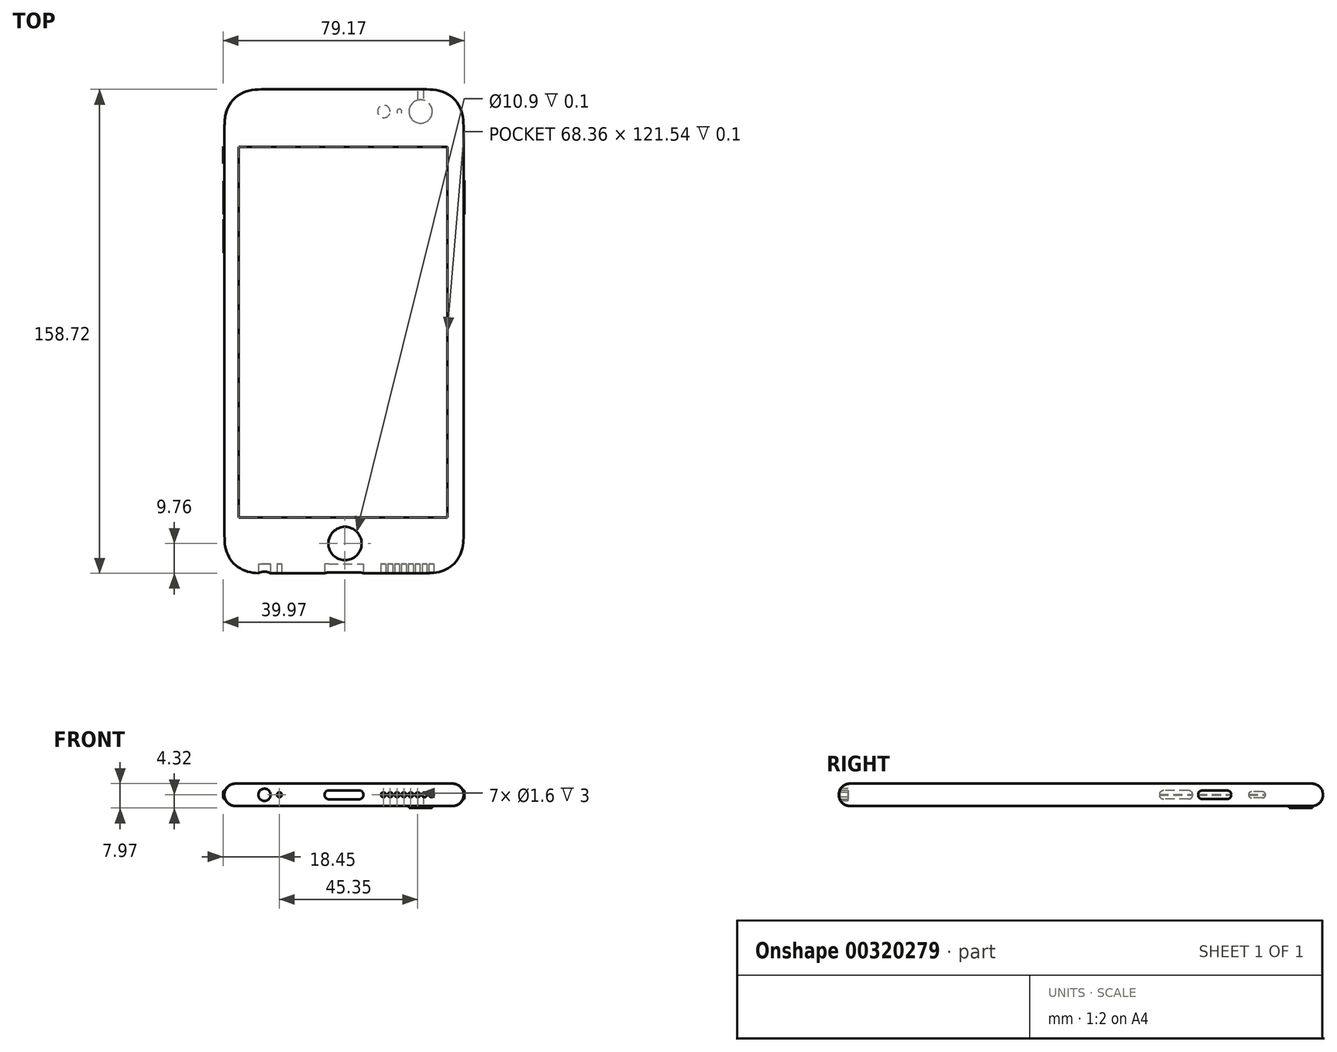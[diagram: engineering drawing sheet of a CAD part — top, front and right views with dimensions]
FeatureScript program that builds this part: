
annotation { "Feature Type Name" : "Feature", "Feature Type Description" : "" }
export const myFeature = defineFeature(function(context is Context, id is Id, definition is map)
    precondition{}
    {
        {
            var Q0;
            Q0=qCreatedBy(makeId("Top.planeOp"),FACE);
            var sketch = newSketch(context, id + "F0", { "sketchPlane" : qUnion([Q0])});
            skLineSegment(sketch, "E0.rect.bottom", {"start": v(25.09, -79.36) * mm, "end": v(-25.09, -79.36) * mm});
            skLineSegment(sketch, "E0.rect.top", {"start": v(25.09, 79.36) * mm, "end": v(-25.09, 79.36) * mm});
            skLineSegment(sketch, "E0.rect.left", {"start": v(39.22, -65.23) * mm, "end": v(39.22, 65.23) * mm});
            skLineSegment(sketch, "E0.rect.right", {"start": v(-39.22, -65.23) * mm, "end": v(-39.22, 65.23) * mm});
            skPoint(sketch, "E0.rect.middle", {"position": v(0, 0) * mm});
            skCircle(sketch, "E1", {"center": v(25.12, 72.09) * mm, "radius": 3.83 * mm});
            skCircle(sketch, "E2", {"center": v(18.16, 72.09) * mm, "radius": 0.8 * mm});
            skCircle(sketch, "E3", {"center": v(13.06, 72.09) * mm, "radius": 2.06 * mm});
            skLineSegment(sketch, "E4", {"start": v(-39.22, 72.1) * mm, "end": v(39.22, 72.1) * mm, "construction": true});
            skPoint(sketch, "E5.visualSharp", {"position": v(-39.22, 79.36) * mm});
            skFitSpline(sketch, "E6", {"points": [v(-25.09, 79.36) * mm, v(-29.02, 79.25) * mm, v(-32.83, 78.38) * mm, v(-36.09, 76.23) * mm, v(-38.24, 72.97) * mm, v(-39.1, 69.16) * mm, v(-39.22, 65.23) * mm], "startDerivative": vector(-8.98, 0) * mm, "endDerivative": vector(0, -8.98) * mm});
            skLineSegment(sketch, "E7", {"start": v(-25.09, 79.36) * mm, "end": v(-39.22, 79.36) * mm, "construction": true});
            skLineSegment(sketch, "E8", {"start": v(-39.22, 79.36) * mm, "end": v(-39.22, 65.23) * mm, "construction": true});
            skLineSegment(sketch, "E9", {"start": v(0, 79.36) * mm, "end": v(0, -79.36) * mm, "construction": true});
            skLineSegment(sketch, "E10", {"start": v(-39.22, 0) * mm, "end": v(39.22, 0) * mm, "construction": true});
            skFitSpline(sketch, "E11.MirrorCS", {"points": [v(25.09, 79.36) * mm, v(29.02, 79.25) * mm, v(32.83, 78.38) * mm, v(36.09, 76.23) * mm, v(38.24, 72.97) * mm, v(39.1, 69.16) * mm, v(39.22, 65.23) * mm], "startDerivative": vector(8.98, 0) * mm, "endDerivative": vector(0, -8.98) * mm});
            skFitSpline(sketch, "E12.MirrorCS", {"points": [v(-25.09, -79.36) * mm, v(-29.02, -79.25) * mm, v(-32.83, -78.38) * mm, v(-36.09, -76.23) * mm, v(-38.24, -72.97) * mm, v(-39.1, -69.16) * mm, v(-39.22, -65.23) * mm], "startDerivative": vector(-8.98, 0) * mm, "endDerivative": vector(0, 8.98) * mm});
            skFitSpline(sketch, "E13.MirrorCS", {"points": [v(25.09, -79.36) * mm, v(29.02, -79.25) * mm, v(32.83, -78.38) * mm, v(36.09, -76.23) * mm, v(38.24, -72.97) * mm, v(39.1, -69.16) * mm, v(39.22, -65.23) * mm], "startDerivative": vector(8.98, 0) * mm, "endDerivative": vector(0, 8.98) * mm});
            skCircle(sketch, "E14", {"center": v(0, 37.36) * mm, "radius": 11 * mm, "construction": true});
            skSolve(sketch);
        }
        {
            var Q0;
            Q0=makeQuery(id+"F0.imprint","IMPRINT",FACE,{"disambiguationData":[TD([[makeQuery(id+"F0.imprint","IMPRINT",EDGE,{"derivedFrom":sQuery(id+"F0.wireOp",EDGE,"E0.rect.bottom")}),-1.0]])]});
            var Q1;
            Q1=makeQuery(id+"F0.imprint","IMPRINT",FACE,{"disambiguationData":[TD([[makeQuery(id+"F0.imprint","IMPRINT",EDGE,{"derivedFrom":sQuery(id+"F0.wireOp",EDGE,"E1")}),1.0]])]});
            var Q2;
            Q2=makeQuery(id+"F0.imprint","IMPRINT",FACE,{"disambiguationData":[TD([[makeQuery(id+"F0.imprint","IMPRINT",EDGE,{"derivedFrom":sQuery(id+"F0.wireOp",EDGE,"E2")}),1.0]])]});
            var Q3;
            Q3=makeQuery(id+"F0.imprint","IMPRINT",FACE,{"disambiguationData":[TD([[makeQuery(id+"F0.imprint","IMPRINT",EDGE,{"derivedFrom":sQuery(id+"F0.wireOp",EDGE,"E3")}),1.0]])]});
            extrude(context, id + "F1", {"entities" : qUnion([Q0, Q1, Q2, Q3]), "depth" : 7.3 * mm});
        }
        {
            var Q0;
            Q0=makeQuery(id+"F0.imprint","IMPRINT",FACE,{"disambiguationData":[TD([[makeQuery(id+"F0.imprint","IMPRINT",EDGE,{"derivedFrom":sQuery(id+"F0.wireOp",EDGE,"E1")}),1.0]])]});
            extrude(context, id + "F2", {"entities" : qUnion([Q0]), "operationType" : NewBodyOperationType.ADD, "oppositeDirection" : true, "depth" : 0.67 * mm});
        }
        {
            var Q0;
            Q0=makeQuery(id+"F0.imprint","IMPRINT",FACE,{"disambiguationData":[TD([[makeQuery(id+"F0.imprint","IMPRINT",EDGE,{"derivedFrom":sQuery(id+"F0.wireOp",EDGE,"E3")}),1.0]])]});
            var Q1;
            Q1=makeQuery(id+"F0.imprint","IMPRINT",FACE,{"disambiguationData":[TD([[makeQuery(id+"F0.imprint","IMPRINT",EDGE,{"derivedFrom":sQuery(id+"F0.wireOp",EDGE,"E2")}),1.0]])]});
            extrude(context, id + "F3", {"entities" : qUnion([Q0, Q1]), "operationType" : NewBodyOperationType.REMOVE, "depth" : 0.1 * mm});
        }
        {
            var Q0;
            Q0=makeQuery(id+"F1.opExtrude","CAP_FACE",FACE,{"disambiguationData":[OSD([sQuery(id+"F0.wireOp",EDGE,"E0.rect.bottom"),sQuery(id+"F0.wireOp",EDGE,"E0.rect.top"),sQuery(id+"F0.wireOp",EDGE,"E0.rect.left"),sQuery(id+"F0.wireOp",EDGE,"E0.rect.right"),sQuery(id+"F0.wireOp",EDGE,"d7852d5b-fe0f-4a90-bdf2-04cff158e1f8.filletArc"),sQuery(id+"F0.wireOp",EDGE,"E5.filletArc"),sQuery(id+"F0.wireOp",EDGE,"7c06d2e9-cdf6-4879-9dee-aab3bc7c6033.filletArc"),sQuery(id+"F0.wireOp",EDGE,"93b3bdb9-dbb8-49f8-8f1e-002f612095da.filletArc")])],"isStart":false});
            var sketch = newSketch(context, id + "F4", { "sketchPlane" : qUnion([Q0])});
            skCircle(sketch, "E15", {"center": v(0.32, -69.6) * mm, "radius": 5.45 * mm});
            skLineSegment(sketch, "E16.bottom", {"start": v(-34.51, 60.44) * mm, "end": v(33.85, 60.44) * mm});
            skLineSegment(sketch, "E16.top", {"start": v(-34.5, -61.1) * mm, "end": v(33.85, -61.1) * mm});
            skLineSegment(sketch, "E16.left", {"start": v(-34.51, 60.44) * mm, "end": v(-34.5, -61.1) * mm});
            skLineSegment(sketch, "E16.right", {"start": v(33.85, 60.44) * mm, "end": v(33.85, -61.1) * mm});
            skSolve(sketch);
        }
        {
            var Q0;
            Q0=makeQuery(id+"F4.imprint","IMPRINT",FACE,{"disambiguationData":[TD([[makeQuery(id+"F4.imprint","IMPRINT",EDGE,{"derivedFrom":sQuery(id+"F4.wireOp",EDGE,"E15")}),1.0]])]});
            extrude(context, id + "F5", {"entities" : qUnion([Q0]), "operationType" : NewBodyOperationType.REMOVE, "oppositeDirection" : true, "depth" : 0.1 * mm});
        }
        {
            var Q0;
            Q0=makeQuery(id+"F4.imprint","IMPRINT",FACE,{"disambiguationData":[TD([[makeQuery(id+"F4.imprint","IMPRINT",EDGE,{"derivedFrom":sQuery(id+"F4.wireOp",EDGE,"E16.bottom")}),-1.0]])]});
            extrude(context, id + "F6", {"entities" : qUnion([Q0]), "operationType" : NewBodyOperationType.REMOVE, "oppositeDirection" : true, "depth" : 0.1 * mm});
        }
        {
            var Q0;
            Q0=makeQuery(id+"F1.opExtrude","SWEPT_FACE",FACE,{"disambiguationData":[OSD([sQuery(id+"F0.wireOp",EDGE,"E0.rect.bottom")])]});
            var sketch = newSketch(context, id + "F7", { "sketchPlane" : qUnion([Q0])});
            skLineSegment(sketch, "E17.0", {"start": v(25.09, 7.3) * mm, "end": v(-25.09, 7.3) * mm, "construction": true});
            skLineSegment(sketch, "E17.1", {"start": v(25.09, 0) * mm, "end": v(-25.09, 0) * mm, "construction": true});
            skLineSegment(sketch, "E17.2", {"start": v(39.22, 7.3) * mm, "end": v(39.22, 0) * mm, "construction": true});
            skLineSegment(sketch, "E17.3", {"start": v(-39.22, 7.3) * mm, "end": v(-39.22, 0) * mm, "construction": true});
            skFitSpline(sketch, "E17.4", {"points": [v(-24.74, 7.3) * mm, v(-29.45, 7.3) * mm, v(-34.16, 7.3) * mm, v(-38.87, 7.3) * mm], "construction": true});
            skFitSpline(sketch, "E17.5", {"points": [v(-24.74, 0) * mm, v(-29.45, 0) * mm, v(-34.16, 0) * mm, v(-38.87, 0) * mm], "construction": true});
            skFitSpline(sketch, "E17.6", {"points": [v(24.74, 0) * mm, v(29.45, 0) * mm, v(34.16, 0) * mm, v(38.87, 0) * mm], "construction": true});
            skFitSpline(sketch, "E17.7", {"points": [v(24.74, 7.3) * mm, v(29.45, 7.3) * mm, v(34.16, 7.3) * mm, v(38.87, 7.3) * mm], "construction": true});
            skLineSegment(sketch, "E18", {"start": v(0, 7.3) * mm, "end": v(0, 0) * mm, "construction": true});
            skLineSegment(sketch, "E19", {"start": v(-39.22, 3.65) * mm, "end": v(-6.4, 3.65) * mm, "construction": true});
            skLineSegment(sketch, "E20", {"start": v(-4.92, 5.12) * mm, "end": v(4.92, 5.12) * mm});
            skLineSegment(sketch, "E21", {"start": v(-4.92, 2.17) * mm, "end": v(4.92, 2.17) * mm});
            skLineSegment(sketch, "E22", {"start": v(-6.4, 3.65) * mm, "end": v(39.22, 3.65) * mm, "construction": true});
            skArc(sketch, "E23", {"start": v(-4.92, 5.13) * mm, "mid": v(-6.4, 3.65) * mm, "end": v(-4.92, 2.17) * mm});
            skArc(sketch, "E24", {"start": v(-4.92, 2.17) * mm, "mid": v(-3.44, 3.65) * mm, "end": v(-4.92, 5.13) * mm, "construction": true});
            skArc(sketch, "E25", {"start": v(4.92, 5.13) * mm, "mid": v(5.96, 4.7) * mm, "end": v(6.4, 3.65) * mm});
            skArc(sketch, "E26", {"start": v(4.92, 2.17) * mm, "mid": v(3.44, 3.65) * mm, "end": v(4.92, 5.13) * mm, "construction": true});
            skArc(sketch, "E27", {"start": v(6.4, 3.65) * mm, "mid": v(5.96, 2.6) * mm, "end": v(4.92, 2.17) * mm});
            skCircle(sketch, "E28", {"center": v(-26.09, 3.65) * mm, "radius": 2 * mm});
            skCircle(sketch, "E29", {"center": v(-21.2, 3.65) * mm, "radius": 0.8 * mm});
            skCircle(sketch, "E30", {"center": v(12.9, 3.65) * mm, "radius": 0.8 * mm});
            skCircle(sketch, "E31.1.0.0", {"center": v(15.15, 3.65) * mm, "radius": 0.8 * mm});
            skCircle(sketch, "E31.2.0.0", {"center": v(17.4, 3.65) * mm, "radius": 0.8 * mm});
            skCircle(sketch, "E31.3.0.0", {"center": v(19.65, 3.65) * mm, "radius": 0.8 * mm});
            skCircle(sketch, "E31.4.0.0", {"center": v(21.9, 3.65) * mm, "radius": 0.8 * mm});
            skCircle(sketch, "E31.5.0.0", {"center": v(24.15, 3.65) * mm, "radius": 0.8 * mm});
            skCircle(sketch, "E31.6.0.0", {"center": v(26.4, 3.65) * mm, "radius": 0.8 * mm});
            skCircle(sketch, "E31.7.0.0", {"center": v(28.65, 3.65) * mm, "radius": 0.8 * mm});
            skLineSegment(sketch, "E31.direction1", {"start": v(12.9, 3.65) * mm, "end": v(15.15, 3.65) * mm, "construction": true});
            skPoint(sketch, "E32", {"position": v(12.1, 3.65) * mm});
            skPoint(sketch, "E33", {"position": v(29.45, 3.65) * mm});
            skLineSegment(sketch, "E34.0", {"start": v(-25.09, 7.3) * mm, "end": v(-25.09, 0) * mm, "construction": true});
            skLineSegment(sketch, "E34.1", {"start": v(25.09, 7.3) * mm, "end": v(25.09, 0) * mm, "construction": true});
            skSolve(sketch);
        }
        {
            var Q0;
            Q0=makeQuery(id+"F1.opExtrude","SWEPT_FACE",FACE,{"disambiguationData":[OSD([sQuery(id+"F0.wireOp",EDGE,"E0.rect.left")])]});
            var sketch = newSketch(context, id + "F8", { "sketchPlane" : qUnion([Q0])});
            skLineSegment(sketch, "E35", {"start": v(-65.23, 2.25) * mm, "end": v(65.23, 2.25) * mm, "construction": true});
            skLineSegment(sketch, "E36", {"start": v(8.97, 4.69) * mm, "end": v(22.34, 4.7) * mm});
            skLineSegment(sketch, "E37", {"start": v(8.97, 2.25) * mm, "end": v(22.34, 2.25) * mm});
            skPoint(sketch, "E38", {"position": v(7.75, 3.47) * mm});
            skPoint(sketch, "E39", {"position": v(23.56, 3.47) * mm});
            skLineSegment(sketch, "E40", {"start": v(39.81, 2.25) * mm, "end": v(47.95, 2.25) * mm});
            skLineSegment(sketch, "E41", {"start": v(39.81, 5.05) * mm, "end": v(39.81, 5.05) * mm});
            skLineSegment(sketch, "E42", {"start": v(39.81, 3.65) * mm, "end": v(47.95, 3.65) * mm, "construction": true});
            skLineSegment(sketch, "E43", {"start": v(39.81, 5.05) * mm, "end": v(47.95, 5.05) * mm});
            skArc(sketch, "E44", {"start": v(47.95, 5.05) * mm, "mid": v(46.55, 3.65) * mm, "end": v(47.95, 2.25) * mm, "construction": true});
            skArc(sketch, "E45", {"start": v(47.95, 2.25) * mm, "mid": v(49.35, 3.65) * mm, "end": v(47.95, 5.05) * mm});
            skArc(sketch, "E46", {"start": v(39.81, 2.25) * mm, "mid": v(41.21, 3.65) * mm, "end": v(39.81, 5.05) * mm, "construction": true});
            skArc(sketch, "E47", {"start": v(39.81, 5.05) * mm, "mid": v(38.41, 3.65) * mm, "end": v(39.81, 2.25) * mm});
            skPoint(sketch, "E48", {"position": v(43.88, 3.65) * mm});
            skPoint(sketch, "E49", {"position": v(38.4, 3.65) * mm});
            skArc(sketch, "E50", {"start": v(8.97, 4.7) * mm, "mid": v(7.75, 3.47) * mm, "end": v(8.97, 2.25) * mm});
            skArc(sketch, "E51", {"start": v(8.97, 2.25) * mm, "mid": v(10.2, 3.47) * mm, "end": v(8.97, 4.7) * mm, "construction": true});
            skArc(sketch, "E52", {"start": v(22.34, 4.7) * mm, "mid": v(21.12, 3.47) * mm, "end": v(22.34, 2.25) * mm, "construction": true});
            skArc(sketch, "E53", {"start": v(22.34, 2.25) * mm, "mid": v(23.56, 3.47) * mm, "end": v(22.34, 4.7) * mm});
            skSolve(sketch);
        }
        {
            var Q0;
            Q0=makeQuery(id+"F1.opExtrude","SWEPT_FACE",FACE,{"disambiguationData":[OSD([sQuery(id+"F0.wireOp",EDGE,"E0.rect.right")])]});
            var sketch = newSketch(context, id + "F9", { "sketchPlane" : qUnion([Q0])});
            skLineSegment(sketch, "E54", {"start": v(-65.23, 3.63) * mm, "end": v(65.23, 3.63) * mm, "construction": true});
            skLineSegment(sketch, "E55", {"start": v(-60.58, 3.65) * mm, "end": v(-54.97, 3.65) * mm, "construction": true});
            skLineSegment(sketch, "E56", {"start": v(-59.6, 2.66) * mm, "end": v(-55.95, 2.66) * mm});
            skLineSegment(sketch, "E57", {"start": v(-59.6, 4.63) * mm, "end": v(-55.95, 4.63) * mm});
            skArc(sketch, "E58", {"start": v(-59.6, 2.66) * mm, "mid": v(-58.61, 3.64) * mm, "end": v(-59.6, 4.63) * mm, "construction": true});
            skArc(sketch, "E59", {"start": v(-59.6, 4.63) * mm, "mid": v(-60.58, 3.64) * mm, "end": v(-59.6, 2.66) * mm});
            skArc(sketch, "E60", {"start": v(-55.95, 2.66) * mm, "mid": v(-54.97, 3.65) * mm, "end": v(-55.95, 4.63) * mm});
            skArc(sketch, "E61", {"start": v(-55.95, 4.63) * mm, "mid": v(-56.94, 3.65) * mm, "end": v(-55.95, 2.66) * mm, "construction": true});
            skPoint(sketch, "E62.first.point", {"position": v(-49.28, 3.63) * mm});
            skPoint(sketch, "E62.second.point", {"position": v(-47.88, 2.23) * mm});
            skPoint(sketch, "E62.third.point", {"position": v(-47.88, 5.03) * mm});
            skPoint(sketch, "E63.first.point", {"position": v(-41.14, 3.63) * mm});
            skPoint(sketch, "E63.second.point", {"position": v(-39.74, 2.23) * mm});
            skPoint(sketch, "E63.third.point", {"position": v(-39.74, 5.03) * mm});
            skLineSegment(sketch, "E64", {"start": v(-47.88, 2.23) * mm, "end": v(-39.74, 2.23) * mm});
            skLineSegment(sketch, "E65", {"start": v(-47.88, 5.03) * mm, "end": v(-39.74, 5.03) * mm});
            skArc(sketch, "E66", {"start": v(-47.88, 5.03) * mm, "mid": v(-49.28, 3.63) * mm, "end": v(-47.88, 2.23) * mm});
            skArc(sketch, "E67", {"start": v(-47.88, 2.23) * mm, "mid": v(-46.48, 3.63) * mm, "end": v(-47.88, 5.03) * mm, "construction": true});
            skArc(sketch, "E68", {"start": v(-39.74, 2.23) * mm, "mid": v(-38.34, 3.63) * mm, "end": v(-39.74, 5.03) * mm});
            skArc(sketch, "E69", {"start": v(-39.74, 5.03) * mm, "mid": v(-41.14, 3.63) * mm, "end": v(-39.74, 2.23) * mm, "construction": true});
            skLineSegment(sketch, "E70", {"start": v(-47.88, 3.63) * mm, "end": v(-39.74, 3.63) * mm, "construction": true});
            skPoint(sketch, "E71", {"position": v(-43.81, 3.63) * mm});
            skLineSegment(sketch, "E72", {"start": v(-35.27, 2.23) * mm, "end": v(-27.13, 2.23) * mm});
            skLineSegment(sketch, "E73", {"start": v(-35.27, 5.03) * mm, "end": v(-27.13, 5.03) * mm});
            skPoint(sketch, "E74.third.point", {"position": v(-36.67, 3.63) * mm});
            skPoint(sketch, "E75.third.point", {"position": v(-25.73, 3.63) * mm});
            skLineSegment(sketch, "E76", {"start": v(-27.13, 3.63) * mm, "end": v(-35.27, 3.63) * mm, "construction": true});
            skPoint(sketch, "E77", {"position": v(-31.2, 3.63) * mm});
            skArc(sketch, "E78", {"start": v(-35.27, 2.23) * mm, "mid": v(-33.87, 3.63) * mm, "end": v(-35.27, 5.03) * mm, "construction": true});
            skArc(sketch, "E79", {"start": v(-35.27, 5.03) * mm, "mid": v(-36.67, 3.63) * mm, "end": v(-35.27, 2.23) * mm});
            skArc(sketch, "E80", {"start": v(-27.13, 5.03) * mm, "mid": v(-28.53, 3.63) * mm, "end": v(-27.13, 2.23) * mm, "construction": true});
            skArc(sketch, "E81", {"start": v(-27.13, 2.23) * mm, "mid": v(-25.73, 3.63) * mm, "end": v(-27.13, 5.03) * mm});
            skSolve(sketch);
        }
        {
            var Q0;
            Q0=makeQuery(id+"F1.opExtrude","CAP_EDGE",EDGE,{"disambiguationData":[OSD([sQuery(id+"F0.wireOp",EDGE,"E0.rect.top")])],"isStart":false});
            var Q1;
            Q1=makeQuery(id+"F1.opExtrude","CAP_EDGE",EDGE,{"disambiguationData":[OSD([sQuery(id+"F0.wireOp",EDGE,"E0.rect.top")])],"isStart":true});
            fillet(context, id + "F10", {"entities" : qUnion([Q0, Q1]), "radius" : (7.1 / 2) * mm, "tangentPropagation" : true, "allowEdgeOverflow" : false});
        }
        {
            var Q0;
            {var subQ0=makeQuery(id+"F1.opExtrude","SWEPT_EDGE",EDGE,{"disambiguationData":[OSD([sQuery(id+"F0.wireOp",EDGE,"E0.rect.bottom"),sQuery(id+"F0.wireOp",EDGE,"E12.MirrorCS")])]});var subQ1=sQuery(id+"F7.wireOp",EDGE,"E28");var subQ3=makeQuery(id+"F7.imprint","INTERSECT",VERTEX,{"disambiguationData":[OD(0.0)],"derivedFrom":[subQ0,subQ1]});Q0=makeQuery(id+"F7.imprint","IMPRINT",FACE,{"disambiguationData":[TD([[makeQuery(id+"F7.imprint","IMPRINT",EDGE,{"disambiguationData":[TD([[subQ3,-1.0]])],"derivedFrom":subQ1}),1.0]])]});}
            var Q1;
            Q1=makeQuery(id+"F7.imprint","IMPRINT",FACE,{"disambiguationData":[TD([[makeQuery(id+"F7.imprint","IMPRINT",EDGE,{"derivedFrom":sQuery(id+"F7.wireOp",EDGE,"E29")}),1.0]])]});
            var Q2;
            Q2=makeQuery(id+"F7.imprint","IMPRINT",FACE,{"disambiguationData":[TD([[makeQuery(id+"F7.imprint","IMPRINT",EDGE,{"derivedFrom":sQuery(id+"F7.wireOp",EDGE,"E20")}),-1.0]])]});
            var Q3;
            Q3=makeQuery(id+"F7.imprint","IMPRINT",FACE,{"disambiguationData":[TD([[makeQuery(id+"F7.imprint","IMPRINT",EDGE,{"derivedFrom":sQuery(id+"F7.wireOp",EDGE,"E30")}),1.0]])]});
            var Q4;
            Q4=makeQuery(id+"F7.imprint","IMPRINT",FACE,{"disambiguationData":[TD([[makeQuery(id+"F7.imprint","IMPRINT",EDGE,{"derivedFrom":sQuery(id+"F7.wireOp",EDGE,"E31.1.0.0")}),1.0]])]});
            var Q5;
            Q5=makeQuery(id+"F7.imprint","IMPRINT",FACE,{"disambiguationData":[TD([[makeQuery(id+"F7.imprint","IMPRINT",EDGE,{"derivedFrom":sQuery(id+"F7.wireOp",EDGE,"E31.2.0.0")}),1.0]])]});
            var Q6;
            Q6=makeQuery(id+"F7.imprint","IMPRINT",FACE,{"disambiguationData":[TD([[makeQuery(id+"F7.imprint","IMPRINT",EDGE,{"derivedFrom":sQuery(id+"F7.wireOp",EDGE,"E31.3.0.0")}),1.0]])]});
            var Q7;
            Q7=makeQuery(id+"F7.imprint","IMPRINT",FACE,{"disambiguationData":[TD([[makeQuery(id+"F7.imprint","IMPRINT",EDGE,{"derivedFrom":sQuery(id+"F7.wireOp",EDGE,"E31.4.0.0")}),1.0]])]});
            var Q8;
            Q8=makeQuery(id+"F7.imprint","IMPRINT",FACE,{"disambiguationData":[TD([[makeQuery(id+"F7.imprint","IMPRINT",EDGE,{"derivedFrom":sQuery(id+"F7.wireOp",EDGE,"E31.5.0.0")}),1.0]])]});
            var Q9;
            Q9=makeQuery(id+"F7.imprint","IMPRINT",FACE,{"disambiguationData":[TD([[makeQuery(id+"F7.imprint","IMPRINT",EDGE,{"derivedFrom":sQuery(id+"F7.wireOp",EDGE,"E31.6.0.0")}),1.0]])]});
            var Q10;
            Q10=makeQuery(id+"F7.imprint","IMPRINT",FACE,{"disambiguationData":[TD([[makeQuery(id+"F7.imprint","IMPRINT",EDGE,{"derivedFrom":sQuery(id+"F7.wireOp",EDGE,"E31.7.0.0")}),1.0]])]});
            var Q11;
            {var subQ0=makeQuery(id+"F1.opExtrude","SWEPT_EDGE",EDGE,{"disambiguationData":[OSD([sQuery(id+"F0.wireOp",EDGE,"E0.rect.bottom"),sQuery(id+"F0.wireOp",EDGE,"E12.MirrorCS")])]});var subQ1=sQuery(id+"F7.wireOp",EDGE,"E28");var subQ3=makeQuery(id+"F7.imprint","INTERSECT",VERTEX,{"disambiguationData":[OD(0.0)],"derivedFrom":[subQ0,subQ1]});Q11=makeQuery(id+"F7.imprint","IMPRINT",FACE,{"disambiguationData":[TD([[makeQuery(id+"F7.imprint","IMPRINT",EDGE,{"disambiguationData":[TD([[subQ3,1.0]])],"derivedFrom":subQ1}),1.0]])]});}
            extrude(context, id + "F11", {"entities" : qUnion([Q0, Q1, Q2, Q3, Q4, Q5, Q6, Q7, Q8, Q9, Q10, Q11]), "oppositeDirection" : true, "depth" : 3 * mm, "hasSecondDirection" : true, "secondDirectionOppositeDirection" : false, "secondDirectionDepth" : 1 * mm});
        }
        {
            var Q0;
            Q0=makeQuery(id+"F11.opExtrude","SWEPT_BODY",BODY,{"disambiguationData":[OSD([sQuery(id+"F7.wireOp",EDGE,"E28")])]});
            var Q1;
            Q1=makeQuery(id+"F11.opExtrude","SWEPT_BODY",BODY,{"disambiguationData":[OSD([sQuery(id+"F7.wireOp",EDGE,"E29")])]});
            var Q2;
            Q2=makeQuery(id+"F11.opExtrude","SWEPT_BODY",BODY,{"disambiguationData":[OSD([sQuery(id+"F7.wireOp",EDGE,"E30")])]});
            var Q3;
            Q3=makeQuery(id+"F11.opExtrude","SWEPT_BODY",BODY,{"disambiguationData":[OSD([sQuery(id+"F7.wireOp",EDGE,"E31.1.0.0")])]});
            var Q4;
            Q4=makeQuery(id+"F11.opExtrude","SWEPT_BODY",BODY,{"disambiguationData":[OSD([sQuery(id+"F7.wireOp",EDGE,"E31.2.0.0")])]});
            var Q5;
            Q5=makeQuery(id+"F11.opExtrude","SWEPT_BODY",BODY,{"disambiguationData":[OSD([sQuery(id+"F7.wireOp",EDGE,"E31.3.0.0")])]});
            var Q6;
            Q6=makeQuery(id+"F11.opExtrude","SWEPT_BODY",BODY,{"disambiguationData":[OSD([sQuery(id+"F7.wireOp",EDGE,"E31.4.0.0")])]});
            var Q7;
            Q7=makeQuery(id+"F11.opExtrude","SWEPT_BODY",BODY,{"disambiguationData":[OSD([sQuery(id+"F7.wireOp",EDGE,"E31.5.0.0")])]});
            var Q8;
            Q8=makeQuery(id+"F11.opExtrude","SWEPT_BODY",BODY,{"disambiguationData":[OSD([sQuery(id+"F7.wireOp",EDGE,"E31.6.0.0")])]});
            var Q9;
            Q9=makeQuery(id+"F11.opExtrude","SWEPT_BODY",BODY,{"disambiguationData":[OSD([sQuery(id+"F7.wireOp",EDGE,"E31.7.0.0")])]});
            var Q10;
            Q10=makeQuery(id+"F11.opExtrude","SWEPT_BODY",BODY,{"disambiguationData":[OSD([sQuery(id+"F7.wireOp",EDGE,"E20"),sQuery(id+"F7.wireOp",EDGE,"E21"),sQuery(id+"F7.wireOp",EDGE,"E23"),sQuery(id+"F7.wireOp",EDGE,"E25"),sQuery(id+"F7.wireOp",EDGE,"E27")])]});
            var Q11;
            Q11=makeQuery(id+"F1.opExtrude","SWEPT_BODY",BODY,{"disambiguationData":[OSD([sQuery(id+"F0.wireOp",EDGE,"E0.rect.bottom"),sQuery(id+"F0.wireOp",EDGE,"E0.rect.top"),sQuery(id+"F0.wireOp",EDGE,"E0.rect.left"),sQuery(id+"F0.wireOp",EDGE,"E0.rect.right"),sQuery(id+"F0.wireOp",EDGE,"E6"),sQuery(id+"F0.wireOp",EDGE,"E11.MirrorCS"),sQuery(id+"F0.wireOp",EDGE,"E12.MirrorCS"),sQuery(id+"F0.wireOp",EDGE,"E13.MirrorCS")])]});
            booleanBodies(context, id + "F12", {"operationType" : BooleanOperationType.SUBTRACTION, "tools" : qUnion([Q0, Q1, Q2, Q3, Q4, Q5, Q6, Q7, Q8, Q9, Q10]), "targets" : qUnion([Q11])});
        }
        {
            var Q0;
            Q0=makeQuery(id+"F8.imprint","IMPRINT",FACE,{"disambiguationData":[TD([[makeQuery(id+"F8.imprint","IMPRINT",EDGE,{"derivedFrom":sQuery(id+"F8.wireOp",EDGE,"E40")}),1.0]])]});
            extrude(context, id + "F13", {"entities" : qUnion([Q0]), "operationType" : NewBodyOperationType.ADD, "depth" : 0.3 * mm});
        }
        {
            var Q0;
            Q0=makeQuery(id+"F9.imprint","IMPRINT",FACE,{"disambiguationData":[TD([[makeQuery(id+"F9.imprint","IMPRINT",EDGE,{"derivedFrom":sQuery(id+"F9.wireOp",EDGE,"E72")}),1.0]])]});
            var Q1;
            Q1=makeQuery(id+"F9.imprint","IMPRINT",FACE,{"disambiguationData":[TD([[makeQuery(id+"F9.imprint","IMPRINT",EDGE,{"derivedFrom":sQuery(id+"F9.wireOp",EDGE,"E64")}),1.0]])]});
            extrude(context, id + "F14", {"entities" : qUnion([Q0, Q1]), "operationType" : NewBodyOperationType.ADD, "depth" : 0.3 * mm});
        }
        {
            var Q0;
            Q0=makeQuery(id+"F9.imprint","IMPRINT",FACE,{"disambiguationData":[TD([[makeQuery(id+"F9.imprint","IMPRINT",EDGE,{"derivedFrom":sQuery(id+"F9.wireOp",EDGE,"E56")}),1.0]])]});
            extrude(context, id + "F15", {"entities" : qUnion([Q0]), "operationType" : NewBodyOperationType.ADD, "depth" : 0.43 * mm});
        }
        {
            var Q0;
            Q0=qCreatedBy(makeId("Top.planeOp"),FACE);
            var sketch = newSketch(context, id + "F16", { "sketchPlane" : qUnion([Q0])});
            skLineSegment(sketch, "E82.bottom", {"start": v(-1.85, 3.11) * mm, "end": v(1.85, 3.11) * mm});
            skLineSegment(sketch, "E82.top", {"start": v(-1.85, -3.12) * mm, "end": v(1.85, -3.12) * mm});
            skLineSegment(sketch, "E82.left", {"start": v(-1.85, 3.11) * mm, "end": v(-1.85, -3.12) * mm});
            skLineSegment(sketch, "E82.right", {"start": v(1.85, 3.11) * mm, "end": v(1.85, -3.12) * mm});
            skPoint(sketch, "E82.middle", {"position": v(0, 0) * mm});
            skSolve(sketch);
        }
    });
